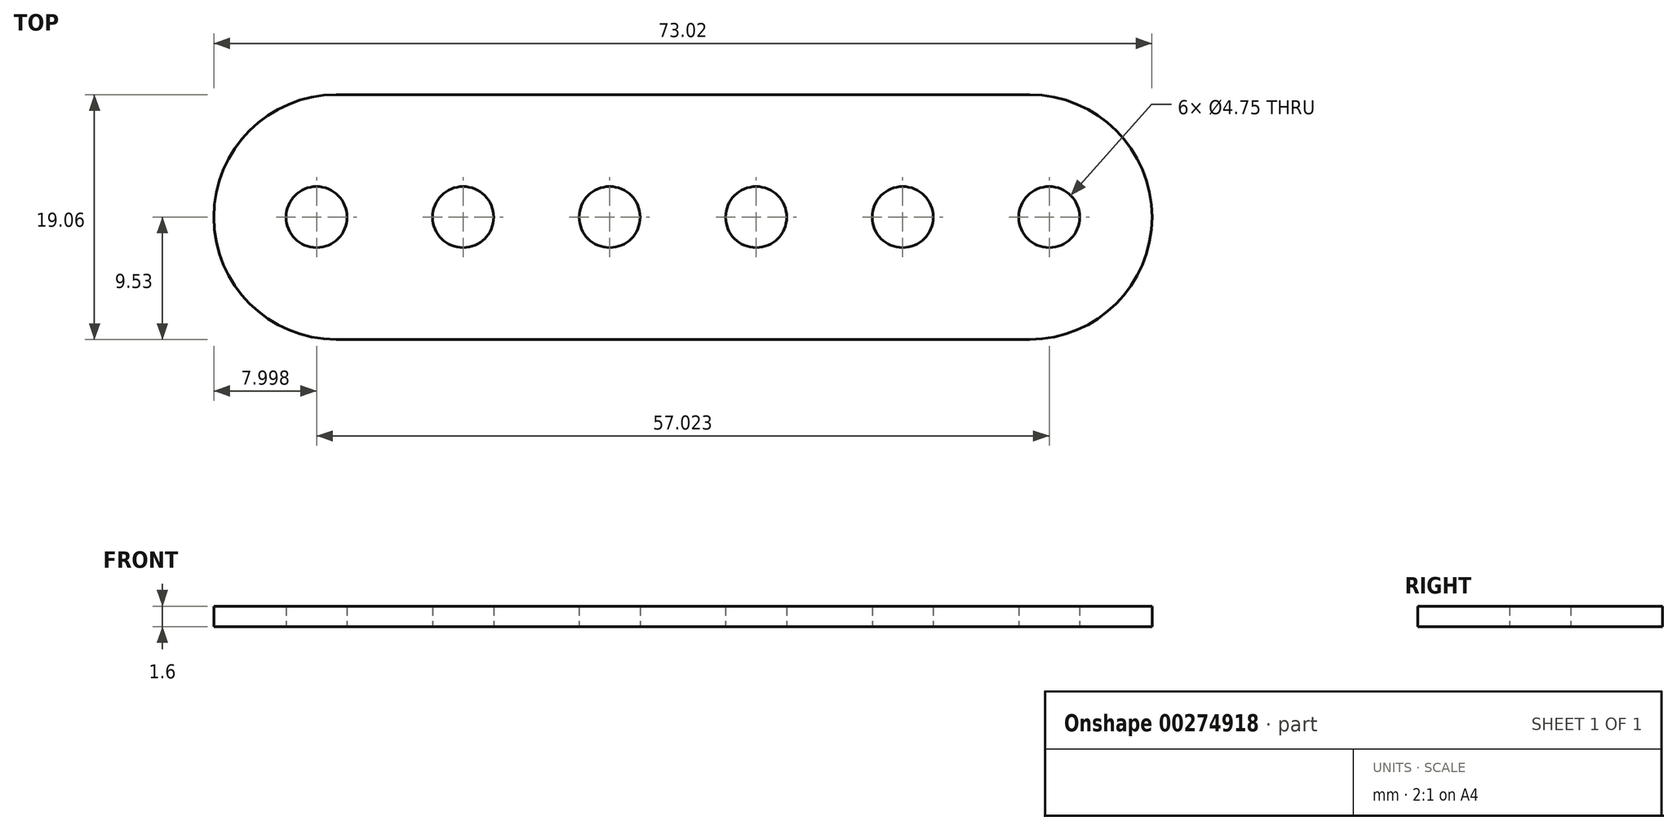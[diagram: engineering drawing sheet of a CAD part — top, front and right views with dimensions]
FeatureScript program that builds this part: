
annotation { "Feature Type Name" : "Feature", "Feature Type Description" : "" }
export const myFeature = defineFeature(function(context is Context, id is Id, definition is map)
    precondition{}
    {
        {
            var Q0;
            Q0=qCreatedBy(makeId("Top.planeOp"),FACE);
            var sketch = newSketch(context, id + "F0", { "sketchPlane" : qUnion([Q0])});
            skCircle(sketch, "E0", {"center": v(5.7, 0) * mm, "radius": 2.37 * mm});
            skCircle(sketch, "E1.1.0.0", {"center": v(17.1, 0) * mm, "radius": 2.37 * mm});
            skCircle(sketch, "E1.2.0.0", {"center": v(28.51, 0) * mm, "radius": 2.37 * mm});
            skLineSegment(sketch, "E1.direction1", {"start": v(5.7, 0) * mm, "end": v(17.1, 0) * mm, "construction": true});
            skLineSegment(sketch, "E2", {"start": v(0, 9.52) * mm, "end": v(26.99, 9.53) * mm});
            skArc(sketch, "E3", {"start": v(36.51, 0) * mm, "mid": v(33.72, 6.74) * mm, "end": v(26.99, 9.53) * mm});
            skLineSegment(sketch, "E4.MirrorCS", {"start": v(0, -9.53) * mm, "end": v(26.99, -9.53) * mm});
            skArc(sketch, "E5.MirrorCS", {"start": v(36.51, 0) * mm, "mid": v(33.72, -6.74) * mm, "end": v(26.99, -9.53) * mm});
            skCircle(sketch, "E6.MirrorC", {"center": v(-5.7, 0) * mm, "radius": 2.37 * mm});
            skCircle(sketch, "E7.MirrorC", {"center": v(-17.1, 0) * mm, "radius": 2.37 * mm});
            skCircle(sketch, "E8.MirrorC", {"center": v(-28.51, 0) * mm, "radius": 2.37 * mm});
            skArc(sketch, "E9.MirrorCS", {"start": v(-36.51, 0) * mm, "mid": v(-33.72, -6.74) * mm, "end": v(-26.99, -9.53) * mm});
            skLineSegment(sketch, "E10.MirrorCS", {"start": v(0, -9.53) * mm, "end": v(-26.99, -9.53) * mm});
            skArc(sketch, "E11.MirrorCS", {"start": v(-36.51, 0) * mm, "mid": v(-33.72, 6.74) * mm, "end": v(-26.99, 9.53) * mm});
            skLineSegment(sketch, "E12.MirrorCS", {"start": v(0, 9.52) * mm, "end": v(-26.99, 9.53) * mm});
            skLineSegment(sketch, "E13.MirrorCS", {"start": v(-5.7, 0) * mm, "end": v(-17.1, 0) * mm, "construction": true});
            skSolve(sketch);
        }
        {
            var Q0;
            Q0 = qSketchRegion(id + "F0", true);
            extrude(context, id + "F1", {"entities" : qUnion([Q0]), "depth" : 1.6 * mm});
        }
    });
